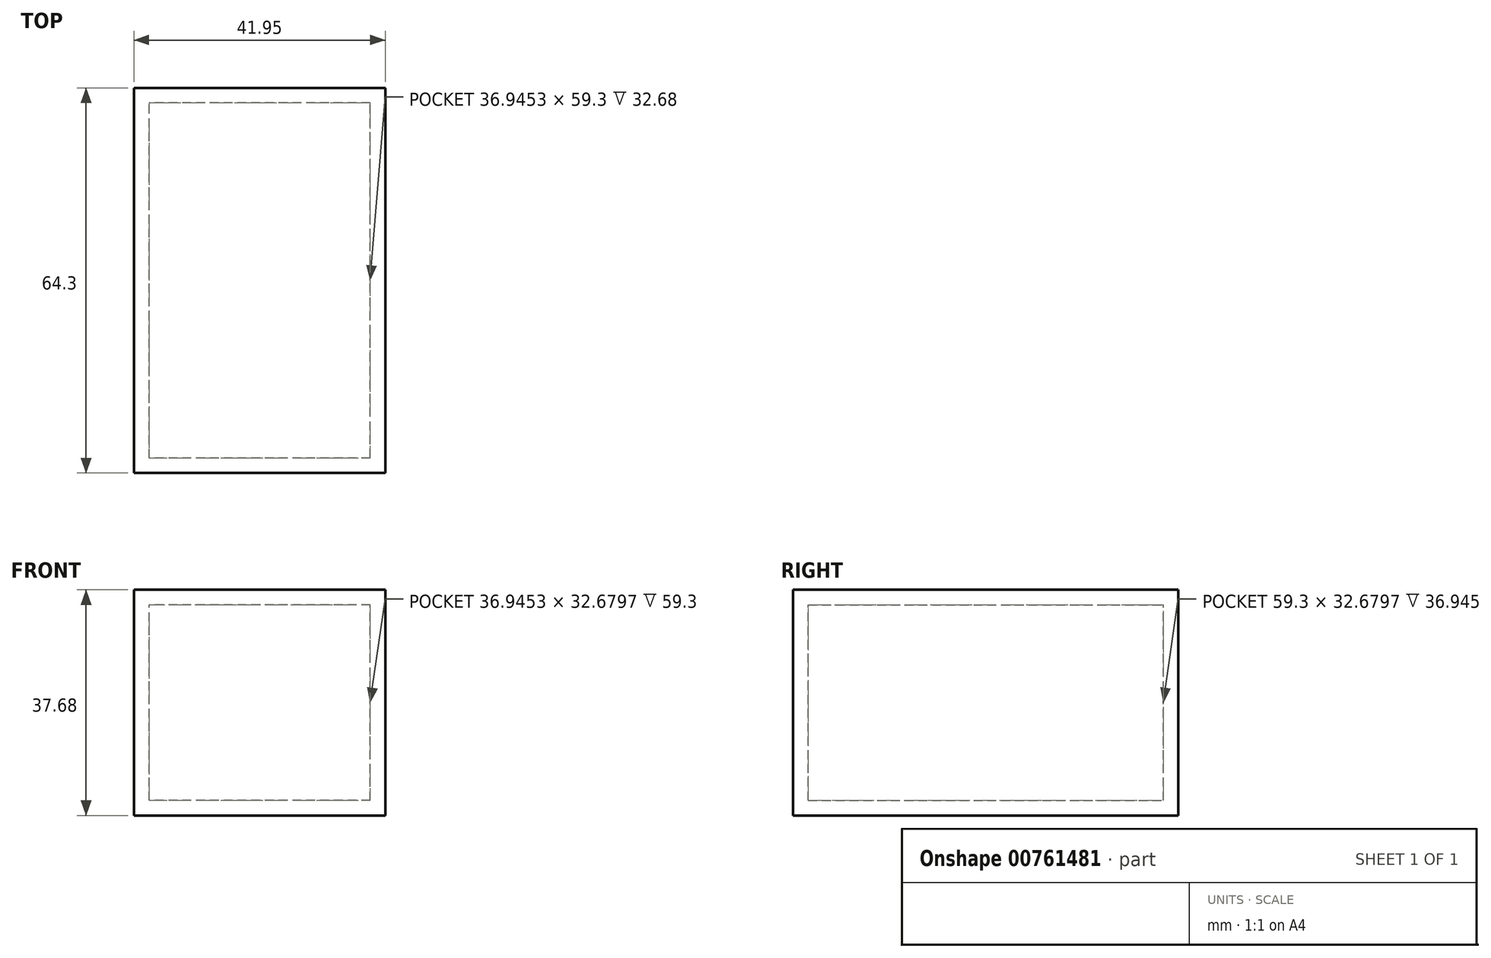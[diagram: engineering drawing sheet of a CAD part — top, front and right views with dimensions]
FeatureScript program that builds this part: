
annotation { "Feature Type Name" : "Feature", "Feature Type Description" : "" }
export const myFeature = defineFeature(function(context is Context, id is Id, definition is map)
    precondition{}
    {
        {
            var Q0;
            Q0=qCreatedBy(makeId("Front.planeOp"),FACE);
            var sketch = newSketch(context, id + "F0", { "sketchPlane" : qUnion([Q0])});
            skLineSegment(sketch, "E0.bottom", {"start": v(0, 0) * mm, "end": v(-41.95, 0) * mm});
            skLineSegment(sketch, "E0.top", {"start": v(0, 37.68) * mm, "end": v(-41.95, 37.68) * mm});
            skLineSegment(sketch, "E0.left", {"start": v(0, 0) * mm, "end": v(0, 37.68) * mm});
            skLineSegment(sketch, "E0.right", {"start": v(-41.95, 0) * mm, "end": v(-41.95, 37.68) * mm});
            skSolve(sketch);
        }
        {
            var Q0;
            Q0=makeQuery(id+"F0.imprint","IMPRINT",FACE,{"disambiguationData":[TD([[makeQuery(id+"F0.imprint","IMPRINT",EDGE,{"derivedFrom":sQuery(id+"F0.wireOp",EDGE,"E0.bottom")}),-1.0]])]});
            extrude(context, id + "F1", {"entities" : qUnion([Q0]), "depth" : 64.3 * mm, "offsetDistance" : 25 * mm});
        }
        {
            var Q0;
            Q0=makeQuery(id+"F1.opExtrude","SWEPT_FACE",FACE,{"disambiguationData":[OSD([sQuery(id+"F0.wireOp",EDGE,"E0.left")])]});
            var Q1;
            Q1=makeQuery(id+"F1.opExtrude","SWEPT_BODY",BODY,{"disambiguationData":[OSD([sQuery(id+"F0.wireOp",EDGE,"E0.bottom"),sQuery(id+"F0.wireOp",EDGE,"E0.top"),sQuery(id+"F0.wireOp",EDGE,"E0.left"),sQuery(id+"F0.wireOp",EDGE,"E0.right")])]});
            shell(context, id + "F2", {"isHollow" : true, "entities" : qUnion([Q0]), "parts" : qUnion([Q1]), "thickness" : 2.5 * mm});
        }
    });
